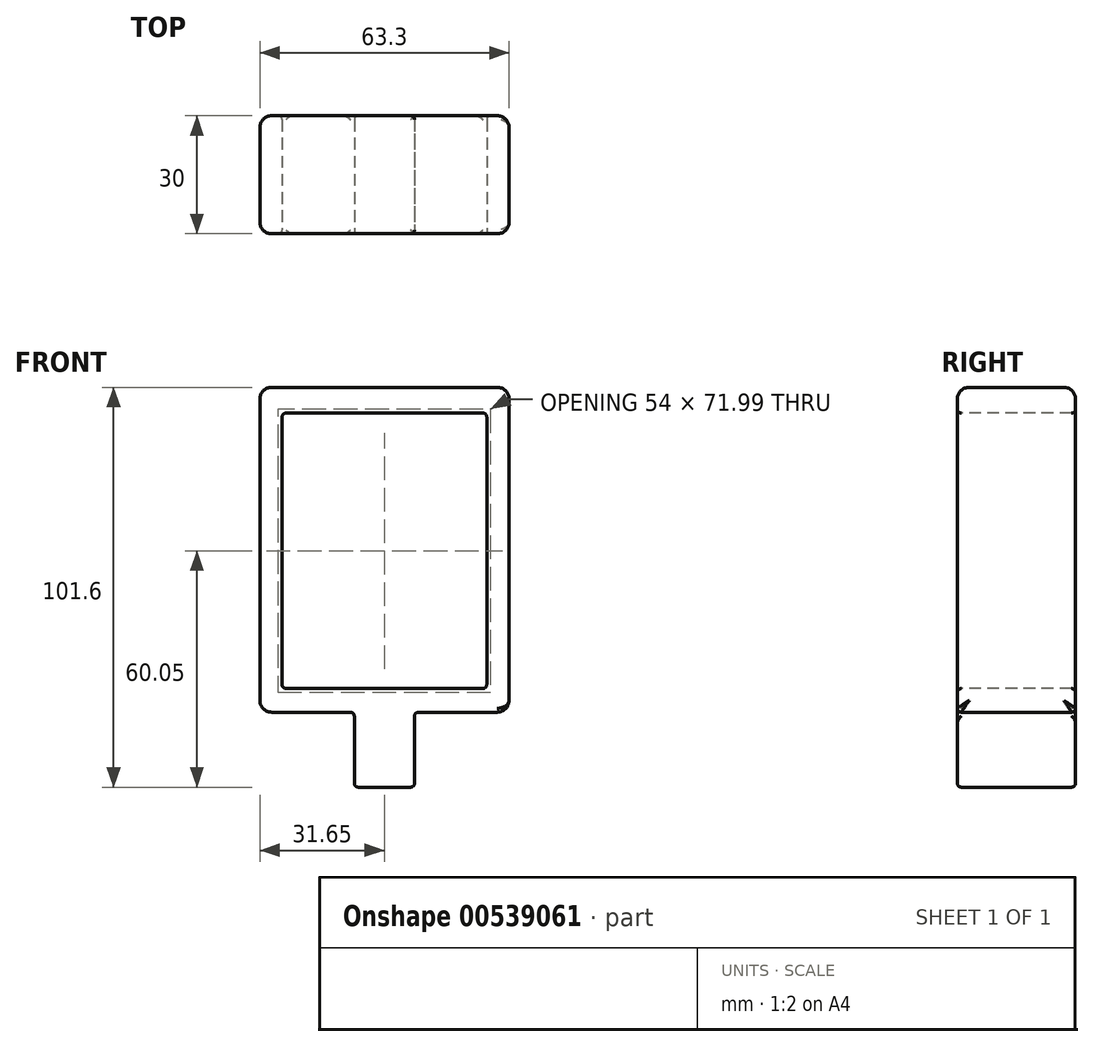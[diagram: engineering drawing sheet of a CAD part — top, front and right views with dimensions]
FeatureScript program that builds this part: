
annotation { "Feature Type Name" : "Feature", "Feature Type Description" : "" }
export const myFeature = defineFeature(function(context is Context, id is Id, definition is map)
    precondition{}
    {
        {
            var Q0;
            Q0=qCreatedBy(makeId("Front.planeOp"),FACE);
            var sketch = newSketch(context, id + "F0", { "sketchPlane" : qUnion([Q0])});
            skLineSegment(sketch, "E0", {"start": v(0, 0) * mm, "end": v(-7.65, 0) * mm});
            skLineSegment(sketch, "E1", {"start": v(-7.65, 0) * mm, "end": v(-7.65, 19.05) * mm});
            skLineSegment(sketch, "E2", {"start": v(-7.65, 19.05) * mm, "end": v(-31.65, 19.05) * mm});
            skLineSegment(sketch, "E3", {"start": v(-31.65, 19.05) * mm, "end": v(-31.65, 101.6) * mm});
            skLineSegment(sketch, "E4", {"start": v(-31.65, 101.6) * mm, "end": v(0, 101.6) * mm});
            skLineSegment(sketch, "E5", {"start": v(0, 101.6) * mm, "end": v(0, 0) * mm});
            skLineSegment(sketch, "E6.MirrorCS", {"start": v(31.65, 101.6) * mm, "end": v(0, 101.6) * mm});
            skLineSegment(sketch, "E7.MirrorCS", {"start": v(31.65, 19.05) * mm, "end": v(31.65, 101.6) * mm});
            skLineSegment(sketch, "E8.MirrorCS", {"start": v(7.65, 19.05) * mm, "end": v(31.65, 19.05) * mm});
            skLineSegment(sketch, "E9.MirrorCS", {"start": v(7.65, 0) * mm, "end": v(7.65, 19.05) * mm});
            skLineSegment(sketch, "E10.MirrorCS", {"start": v(0, 0) * mm, "end": v(7.65, 0) * mm});
            skSolve(sketch);
        }
        {
            var Q0;
            Q0=qSketchRegion(id+"F0",true);
            extrude(context, id + "F1", {"entities" : qUnion([Q0]), "oppositeDirection" : true, "depth" : 30 * mm, "offsetDistance" : 25 * mm});
        }
        {
            var Q0;
            Q0=makeQuery(id+"F1.opExtrude","CAP_FACE",FACE,{"disambiguationData":[OSD([sQuery(id+"F0.wireOp",EDGE,"E0"),sQuery(id+"F0.wireOp",EDGE,"E1"),sQuery(id+"F0.wireOp",EDGE,"E2"),sQuery(id+"F0.wireOp",EDGE,"E3"),sQuery(id+"F0.wireOp",EDGE,"E4"),sQuery(id+"F0.wireOp",EDGE,"E6.MirrorCS"),sQuery(id+"F0.wireOp",EDGE,"E7.MirrorCS"),sQuery(id+"F0.wireOp",EDGE,"E8.MirrorCS"),sQuery(id+"F0.wireOp",EDGE,"E9.MirrorCS"),sQuery(id+"F0.wireOp",EDGE,"E10.MirrorCS")])],"isStart":true});
            var sketch = newSketch(context, id + "F2", { "sketchPlane" : qUnion([Q0])});
            skLineSegment(sketch, "E11", {"start": v(0, 25.05) * mm, "end": v(-26, 25.05) * mm});
            skLineSegment(sketch, "E12", {"start": v(-26, 25.05) * mm, "end": v(-26, 95.05) * mm});
            skLineSegment(sketch, "E13", {"start": v(-26, 95.05) * mm, "end": v(0, 95.05) * mm});
            skLineSegment(sketch, "E14.MirrorCS", {"start": v(26, 95.05) * mm, "end": v(0, 95.05) * mm});
            skLineSegment(sketch, "E15.MirrorCS", {"start": v(26, 25.05) * mm, "end": v(26, 95.05) * mm});
            skLineSegment(sketch, "E16.MirrorCS", {"start": v(0, 25.05) * mm, "end": v(26, 25.05) * mm});
            skSolve(sketch);
        }
        {
            var Q0;
            Q0=qSketchRegion(id+"F2",true);
            extrude(context, id + "F3", {"entities" : qUnion([Q0]), "operationType" : NewBodyOperationType.REMOVE, "endBound" : BoundingType.THROUGH_ALL, "oppositeDirection" : true, "depth" : 25 * mm, "offsetDistance" : 25 * mm});
        }
        {
            var Q0;
            Q0=makeQuery(id+"F1.opExtrude","SWEPT_FACE",FACE,{"disambiguationData":[OSD([sQuery(id+"F0.wireOp",EDGE,"E4"),sQuery(id+"F0.wireOp",EDGE,"E6.MirrorCS")])]});
            var Q1;
            Q1=makeQuery(id+"F1.opExtrude","SWEPT_FACE",FACE,{"disambiguationData":[OSD([sQuery(id+"F0.wireOp",EDGE,"E7.MirrorCS")])]});
            var Q2;
            Q2=makeQuery(id+"F1.opExtrude","SWEPT_FACE",FACE,{"disambiguationData":[OSD([sQuery(id+"F0.wireOp",EDGE,"E3")])]});
            fillet(context, id + "F4", {"entities" : qUnion([Q0, Q1, Q2]), "radius" : 3 * mm, "tangentPropagation" : true, "allowEdgeOverflow" : false});
        }
        {
            var Q0;
            Q0=makeQuery(id+"F1.opExtrude","SWEPT_FACE",FACE,{"disambiguationData":[OSD([sQuery(id+"F0.wireOp",EDGE,"E1")])]});
            var Q1;
            Q1=makeQuery(id+"F1.opExtrude","SWEPT_FACE",FACE,{"disambiguationData":[OSD([sQuery(id+"F0.wireOp",EDGE,"E8.MirrorCS")])]});
            var Q2;
            Q2=makeQuery(id+"F1.opExtrude","SWEPT_FACE",FACE,{"disambiguationData":[OSD([sQuery(id+"F0.wireOp",EDGE,"E0"),sQuery(id+"F0.wireOp",EDGE,"E10.MirrorCS")])]});
            var Q3;
            Q3=makeQuery(id+"F3.boolean.opBoolean","COPY",FACE,{"derivedFrom":makeQuery(id+"F3.opExtrude","SWEPT_FACE",FACE,{"disambiguationData":[OSD([sQuery(id+"F2.wireOp",EDGE,"E12")])]})});
            var Q4;
            Q4=makeQuery(id+"F3.boolean.opBoolean","COPY",FACE,{"derivedFrom":makeQuery(id+"F3.opExtrude","SWEPT_FACE",FACE,{"disambiguationData":[OSD([sQuery(id+"F2.wireOp",EDGE,"E15.MirrorCS")])]})});
            fillet(context, id + "F5", {"entities" : qUnion([Q0, Q1, Q2, Q3, Q4]), "radius" : 1 * mm, "tangentPropagation" : true, "allowEdgeOverflow" : false});
        }
    });
